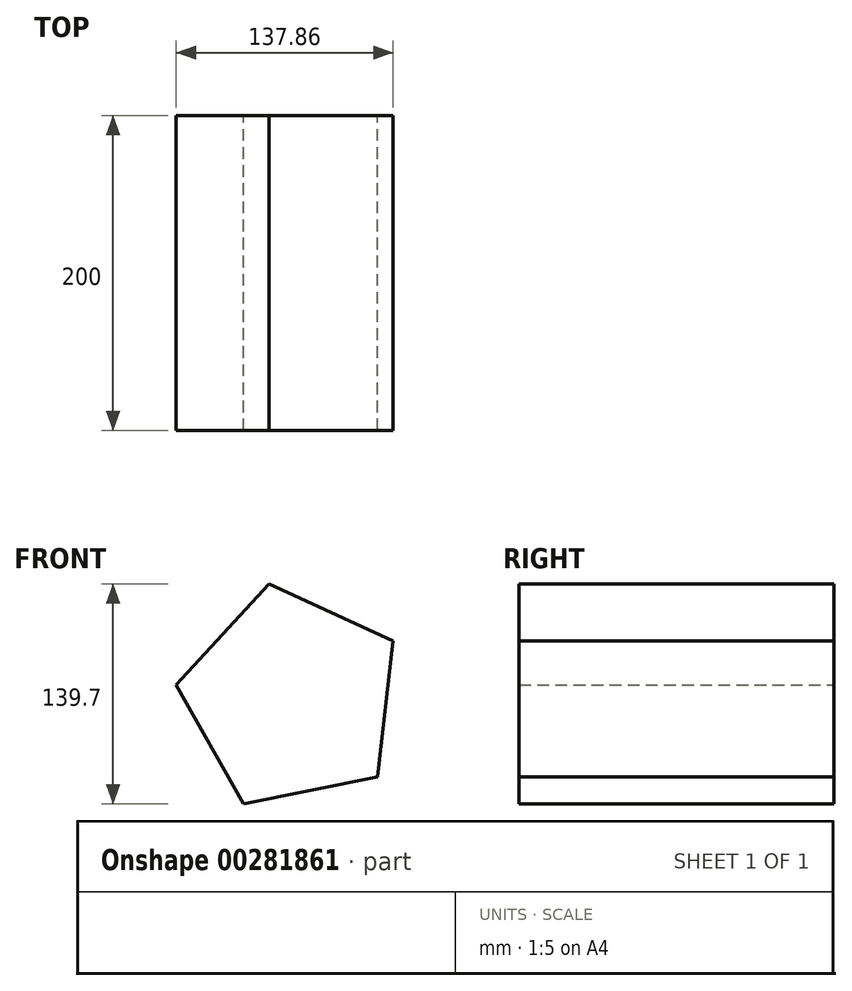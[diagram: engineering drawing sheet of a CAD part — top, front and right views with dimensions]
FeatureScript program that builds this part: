
annotation { "Feature Type Name" : "Feature", "Feature Type Description" : "" }
export const myFeature = defineFeature(function(context is Context, id is Id, definition is map)
    precondition{}
    {
        {
            var Q0;
            Q0=qCreatedBy(makeId("Front.planeOp"),FACE);
            var sketch = newSketch(context, id + "F0", { "sketchPlane" : qUnion([Q0])});
            skCircle(sketch, "E0.cCircle", {"center": v(0, 0) * mm, "radius": 73.93 * mm, "construction": true});
            skLineSegment(sketch, "E0.0", {"start": v(64.42, 36.29) * mm, "end": v(54.42, -50.05) * mm});
            skLineSegment(sketch, "E0.1", {"start": v(54.42, -50.05) * mm, "end": v(-30.78, -67.22) * mm});
            skLineSegment(sketch, "E0.2", {"start": v(-30.78, -67.22) * mm, "end": v(-73.44, 8.5) * mm});
            skLineSegment(sketch, "E0.3", {"start": v(-73.44, 8.5) * mm, "end": v(-14.6, 72.48) * mm});
            skLineSegment(sketch, "E0.4", {"start": v(-14.6, 72.48) * mm, "end": v(64.42, 36.29) * mm});
            skSolve(sketch);
        }
        {
            var Q0;
            Q0=makeQuery(id+"F0.imprint","IMPRINT",FACE,{"disambiguationData":[TD([[makeQuery(id+"F0.imprint","IMPRINT",EDGE,{"derivedFrom":sQuery(id+"F0.wireOp",EDGE,"E0.0")}),-1.0]])]});
            extrude(context, id + "F1", {"entities" : qUnion([Q0]), "depth" : 200 * mm});
        }
    });
